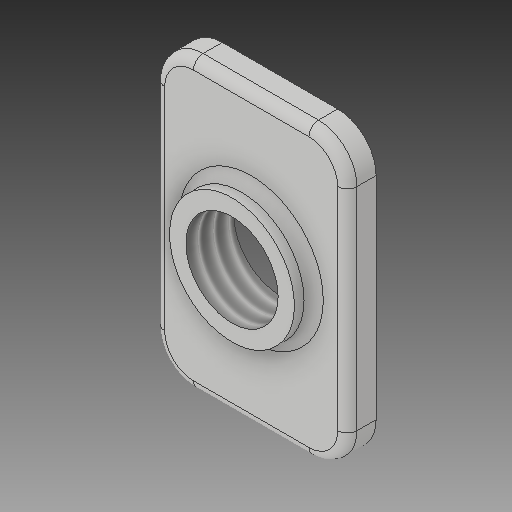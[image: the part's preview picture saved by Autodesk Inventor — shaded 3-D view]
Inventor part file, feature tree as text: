
AUTODESK INVENTOR PART (.ipt)
format: ipt  version: 2017 (Build 210142000, 142)  size: 162,304 bytes
history: native  units: mm
features: other x3, sketch x2
ambient origin geometry x8: Origin, YZ Plane, XZ Plane, XY Plane, X Axis, Y Axis, Z Axis, Center Point
bodies: Solid1 (feature_tree)
feature tree (5):
  other  "M5 Tee Nut_MIR.ipt"
  other  "Solid1::M5 Tee Nut_MIR.ipt"
  other  "TaggingFeature1"
  sketch  "Sketch1"  dims[d0=10.0mm]
  sketch  "Sketch2"
